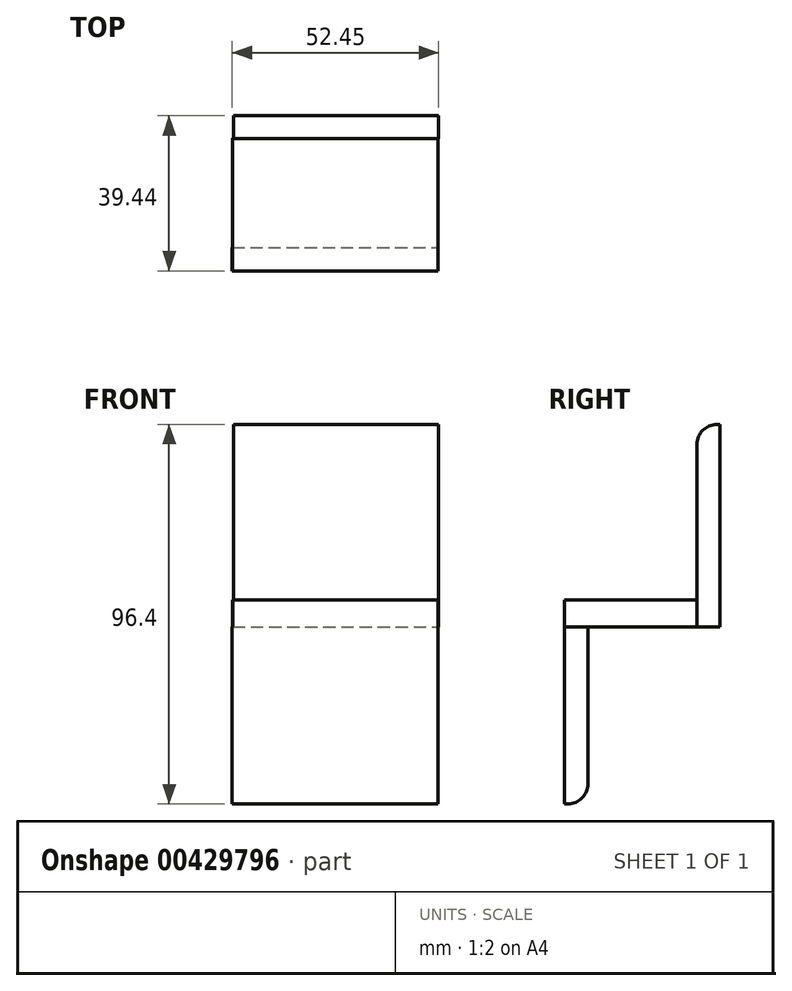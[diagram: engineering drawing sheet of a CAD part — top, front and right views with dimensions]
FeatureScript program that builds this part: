
annotation { "Feature Type Name" : "Feature", "Feature Type Description" : "" }
export const myFeature = defineFeature(function(context is Context, id is Id, definition is map)
    precondition{}
    {
        {
            var Q0;
            Q0=qCreatedBy(makeId("Top.planeOp"),FACE);
            var sketch = newSketch(context, id + "F0", { "sketchPlane" : qUnion([Q0])});
            skLineSegment(sketch, "E0.bottom", {"start": v(-27, 39.44) * mm, "end": v(25.2, 39.44) * mm});
            skLineSegment(sketch, "E0.top", {"start": v(-27, 33.6) * mm, "end": v(25.2, 33.6) * mm});
            skLineSegment(sketch, "E0.left", {"start": v(-27, 39.44) * mm, "end": v(-27, 33.6) * mm});
            skLineSegment(sketch, "E0.right", {"start": v(25.2, 39.44) * mm, "end": v(25.2, 33.6) * mm});
            skSolve(sketch);
        }
        {
            var Q0;
            Q0=makeQuery(id+"F0.imprint","IMPRINT",FACE,{"disambiguationData":[TD([[makeQuery(id+"F0.imprint","IMPRINT",EDGE,{"derivedFrom":sQuery(id+"F0.wireOp",EDGE,"E0.bottom")}),-1.0]])]});
            extrude(context, id + "F1", {"entities" : qUnion([Q0]), "depth" : 51.45 * mm});
        }
        {
            var Q0;
            Q0=qCreatedBy(makeId("Front.planeOp"),FACE);
            var sketch = newSketch(context, id + "F2", { "sketchPlane" : qUnion([Q0])});
            skLineSegment(sketch, "E1.bottom", {"start": v(25.05, 0) * mm, "end": v(-27.15, 0) * mm});
            skLineSegment(sketch, "E1.top", {"start": v(25.05, 6.9) * mm, "end": v(-27.15, 6.9) * mm});
            skLineSegment(sketch, "E1.left", {"start": v(25.05, 0) * mm, "end": v(25.05, 6.9) * mm});
            skLineSegment(sketch, "E1.right", {"start": v(-27.15, 0) * mm, "end": v(-27.15, 6.9) * mm});
            skSolve(sketch);
        }
        {
            var Q0;
            Q0 = qSketchRegion(id + "F2", true);
            extrude(context, id + "F3", {"entities" : qUnion([Q0]), "operationType" : NewBodyOperationType.ADD, "oppositeDirection" : true, "depth" : 33.7 * mm});
        }
        {
            var Q0;
            Q0=qCreatedBy(makeId("Top.planeOp"),FACE);
            var sketch = newSketch(context, id + "F4", { "sketchPlane" : qUnion([Q0])});
            skLineSegment(sketch, "E2.bottom", {"start": v(-27.25, 0) * mm, "end": v(24.96, 0) * mm});
            skLineSegment(sketch, "E2.top", {"start": v(-27.25, 5.92) * mm, "end": v(24.96, 5.92) * mm});
            skLineSegment(sketch, "E2.left", {"start": v(-27.25, 0) * mm, "end": v(-27.25, 5.92) * mm});
            skLineSegment(sketch, "E2.right", {"start": v(24.96, 0) * mm, "end": v(24.96, 5.92) * mm});
            skSolve(sketch);
        }
        {
            var Q0;
            Q0 = qSketchRegion(id + "F4", true);
            extrude(context, id + "F5", {"entities" : qUnion([Q0]), "operationType" : NewBodyOperationType.ADD, "oppositeDirection" : true, "depth" : 44.95 * mm});
        }
        {
            var Q0;
            Q0=makeQuery(id+"F5.opExtrude","CAP_EDGE",EDGE,{"disambiguationData":[OSD([sQuery(id+"F4.wireOp",EDGE,"E2.top")])],"isStart":false});
            fillet(context, id + "F6", {"entities" : qUnion([Q0]), "radius" : 5.08 * mm, "tangentPropagation" : true, "allowEdgeOverflow" : false});
        }
        {
            var Q0;
            Q0=makeQuery(id+"F1.opExtrude","CAP_EDGE",EDGE,{"disambiguationData":[OSD([sQuery(id+"F0.wireOp",EDGE,"E0.top")])],"isStart":false});
            fillet(context, id + "F7", {"entities" : qUnion([Q0]), "radius" : 5.08 * mm, "tangentPropagation" : true, "allowEdgeOverflow" : false});
        }
    });
